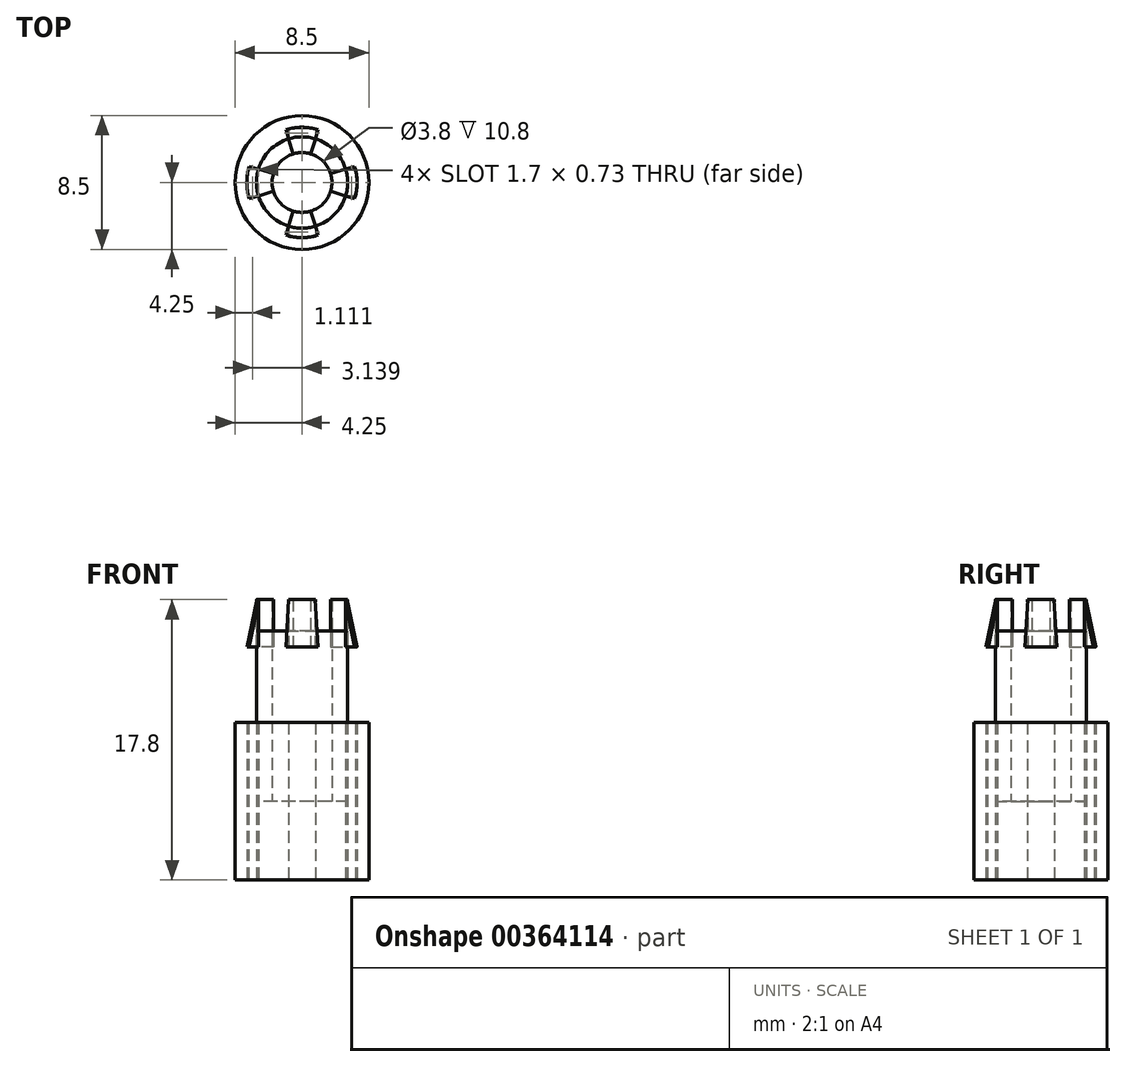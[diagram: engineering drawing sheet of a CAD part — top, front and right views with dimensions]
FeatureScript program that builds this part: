
annotation { "Feature Type Name" : "Feature", "Feature Type Description" : "" }
export const myFeature = defineFeature(function(context is Context, id is Id, definition is map)
    precondition{}
    {
        {
            var Q0;
            Q0=qCreatedBy(makeId("Top.planeOp"),FACE);
            var sketch = newSketch(context, id + "F0", { "sketchPlane" : qUnion([Q0])});
            skCircle(sketch, "E0", {"center": v(0, 0) * mm, "radius": 2.9 * mm});
            skCircle(sketch, "E1", {"center": v(0, 0) * mm, "radius": 4.25 * mm});
            skCircle(sketch, "E2", {"center": v(0, 0) * mm, "radius": 1.9 * mm});
            skLineSegment(sketch, "E3.bottom", {"start": v(-4.25, 4.25) * mm, "end": v(4.25, 4.25) * mm, "construction": true});
            skLineSegment(sketch, "E3.top", {"start": v(-4.25, -4.25) * mm, "end": v(4.25, -4.25) * mm, "construction": true});
            skLineSegment(sketch, "E3.left", {"start": v(-4.25, 4.25) * mm, "end": v(-4.25, -4.25) * mm, "construction": true});
            skLineSegment(sketch, "E3.right", {"start": v(4.25, 4.25) * mm, "end": v(4.25, -4.25) * mm, "construction": true});
            skLineSegment(sketch, "E4", {"start": v(0, 7.12) * mm, "end": v(0, -6.8) * mm, "construction": true});
            skPoint(sketch, "E4.startSnap0", {"position": v(0, 4.25) * mm});
            skLineSegment(sketch, "E5", {"start": v(6.9, 0) * mm, "end": v(-7.5, 0) * mm, "construction": true});
            skArc(sketch, "E6", {"start": v(-0.85, 3.4) * mm, "mid": v(0, 3.5) * mm, "end": v(0.85, 3.4) * mm});
            skArc(sketch, "E7", {"start": v(3.4, 0.85) * mm, "mid": v(3.5, 0) * mm, "end": v(3.4, -0.85) * mm});
            skArc(sketch, "E8", {"start": v(0.85, -3.4) * mm, "mid": v(0, -3.5) * mm, "end": v(-0.85, -3.4) * mm});
            skArc(sketch, "E9", {"start": v(-3.4, -0.85) * mm, "mid": v(-3.5, 0) * mm, "end": v(-3.4, 0.85) * mm});
            skLineSegment(sketch, "E10", {"start": v(-0.85, 3.4) * mm, "end": v(-0.85, 2.77) * mm});
            skLineSegment(sketch, "E11", {"start": v(0.85, 3.4) * mm, "end": v(0.85, 2.77) * mm});
            skLineSegment(sketch, "E12", {"start": v(3.4, 0.85) * mm, "end": v(2.77, 0.85) * mm});
            skLineSegment(sketch, "E13", {"start": v(3.4, -0.85) * mm, "end": v(2.77, -0.85) * mm});
            skLineSegment(sketch, "E14", {"start": v(0.85, -2.77) * mm, "end": v(0.85, -3.4) * mm});
            skLineSegment(sketch, "E15", {"start": v(-0.85, -2.77) * mm, "end": v(-0.85, -3.4) * mm});
            skLineSegment(sketch, "E16", {"start": v(-3.4, 0.85) * mm, "end": v(-2.77, 0.85) * mm});
            skLineSegment(sketch, "E17", {"start": v(-3.4, -0.85) * mm, "end": v(-2.77, -0.85) * mm});
            skLineSegment(sketch, "E18", {"start": v(0, 0) * mm, "end": v(-0.85, 2.77) * mm, "construction": true});
            skLineSegment(sketch, "E19", {"start": v(0, 0) * mm, "end": v(0.85, 2.77) * mm, "construction": true});
            skLineSegment(sketch, "E20", {"start": v(2.77, 0.85) * mm, "end": v(0, 0) * mm, "construction": true});
            skLineSegment(sketch, "E21", {"start": v(0, 0) * mm, "end": v(2.77, -0.85) * mm, "construction": true});
            skLineSegment(sketch, "E22", {"start": v(0, 0) * mm, "end": v(0.85, -2.77) * mm, "construction": true});
            skLineSegment(sketch, "E23", {"start": v(-0.85, -2.77) * mm, "end": v(0, 0) * mm, "construction": true});
            skLineSegment(sketch, "E24", {"start": v(0, 0) * mm, "end": v(-2.77, -0.85) * mm, "construction": true});
            skLineSegment(sketch, "E25", {"start": v(0, 0) * mm, "end": v(-2.77, 0.85) * mm, "construction": true});
            skLineSegment(sketch, "E26", {"start": v(-1.82, 0.56) * mm, "end": v(-2.77, 0.85) * mm});
            skLineSegment(sketch, "E27", {"start": v(-1.82, -0.56) * mm, "end": v(-2.77, -0.85) * mm});
            skLineSegment(sketch, "E28", {"start": v(-0.56, -1.82) * mm, "end": v(-0.85, -2.77) * mm});
            skLineSegment(sketch, "E29", {"start": v(0.85, -2.77) * mm, "end": v(0.56, -1.82) * mm});
            skLineSegment(sketch, "E30", {"start": v(2.77, -0.85) * mm, "end": v(1.82, -0.56) * mm});
            skLineSegment(sketch, "E31", {"start": v(1.82, 0.56) * mm, "end": v(2.77, 0.85) * mm});
            skLineSegment(sketch, "E32", {"start": v(0.56, 1.82) * mm, "end": v(0.85, 2.77) * mm});
            skLineSegment(sketch, "E33", {"start": v(-0.56, 1.82) * mm, "end": v(-0.85, 2.77) * mm});
            skLineSegment(sketch, "E34", {"start": v(0, 0) * mm, "end": v(-4.25, 4.25) * mm, "construction": true});
            skLineSegment(sketch, "E35", {"start": v(0, 0) * mm, "end": v(4.25, 4.25) * mm, "construction": true});
            skLineSegment(sketch, "E36", {"start": v(0, 0) * mm, "end": v(4.25, -4.25) * mm, "construction": true});
            skLineSegment(sketch, "E37", {"start": v(0, 0) * mm, "end": v(-4.25, -4.25) * mm, "construction": true});
            skSolve(sketch);
        }
        {
            var Q0;
            Q0=makeQuery(id+"F0.imprint","IMPRINT",FACE,{"disambiguationData":[TD([[makeQuery(id+"F0.imprint","IMPRINT",EDGE,{"derivedFrom":sQuery(id+"F0.wireOp",EDGE,"E1")}),1.0]])]});
            var Q1;
            {var subQ2=sQuery(id+"F0.wireOp",EDGE,"E30");Q1=makeQuery(id+"F0.imprint","IMPRINT",FACE,{"disambiguationData":[TD([[makeQuery(id+"F0.imprint","IMPRINT",EDGE,{"derivedFrom":subQ2}),-1.0]])]});}
            var Q2;
            {var subQ2=sQuery(id+"F0.wireOp",EDGE,"E31");Q2=makeQuery(id+"F0.imprint","IMPRINT",FACE,{"disambiguationData":[TD([[makeQuery(id+"F0.imprint","IMPRINT",EDGE,{"derivedFrom":subQ2}),1.0]])]});}
            var Q3;
            {var subQ2=sQuery(id+"F0.wireOp",EDGE,"E32");Q3=makeQuery(id+"F0.imprint","IMPRINT",FACE,{"disambiguationData":[TD([[makeQuery(id+"F0.imprint","IMPRINT",EDGE,{"derivedFrom":subQ2}),1.0]])]});}
            var Q4;
            Q4=makeQuery(id+"F0.imprint","IMPRINT",FACE,{"disambiguationData":[TD([[makeQuery(id+"F0.imprint","IMPRINT",EDGE,{"derivedFrom":sQuery(id+"F0.wireOp",EDGE,"E6")}),-1.0]])]});
            var Q5;
            {var subQ2=sQuery(id+"F0.wireOp",EDGE,"E26");Q5=makeQuery(id+"F0.imprint","IMPRINT",FACE,{"disambiguationData":[TD([[makeQuery(id+"F0.imprint","IMPRINT",EDGE,{"derivedFrom":subQ2}),-1.0]])]});}
            var Q6;
            {var subQ0=sQuery(id+"F0.wireOp",EDGE,"E26");Q6=makeQuery(id+"F0.imprint","IMPRINT",FACE,{"disambiguationData":[TD([[makeQuery(id+"F0.imprint","IMPRINT",EDGE,{"derivedFrom":subQ0}),1.0]])]});}
            var Q7;
            Q7=makeQuery(id+"F0.imprint","IMPRINT",FACE,{"disambiguationData":[TD([[makeQuery(id+"F0.imprint","IMPRINT",EDGE,{"derivedFrom":sQuery(id+"F0.wireOp",EDGE,"E9")}),-1.0]])]});
            var Q8;
            {var subQ2=sQuery(id+"F0.wireOp",EDGE,"E27");Q8=makeQuery(id+"F0.imprint","IMPRINT",FACE,{"disambiguationData":[TD([[makeQuery(id+"F0.imprint","IMPRINT",EDGE,{"derivedFrom":subQ2}),1.0]])]});}
            var Q9;
            {var subQ2=sQuery(id+"F0.wireOp",EDGE,"E28");Q9=makeQuery(id+"F0.imprint","IMPRINT",FACE,{"disambiguationData":[TD([[makeQuery(id+"F0.imprint","IMPRINT",EDGE,{"derivedFrom":subQ2}),1.0]])]});}
            var Q10;
            Q10=makeQuery(id+"F0.imprint","IMPRINT",FACE,{"disambiguationData":[TD([[makeQuery(id+"F0.imprint","IMPRINT",EDGE,{"derivedFrom":sQuery(id+"F0.wireOp",EDGE,"E8")}),-1.0]])]});
            var Q11;
            {var subQ2=sQuery(id+"F0.wireOp",EDGE,"E29");Q11=makeQuery(id+"F0.imprint","IMPRINT",FACE,{"disambiguationData":[TD([[makeQuery(id+"F0.imprint","IMPRINT",EDGE,{"derivedFrom":subQ2}),-1.0]])]});}
            var Q12;
            {var subQ0=sQuery(id+"F0.wireOp",EDGE,"E2");var subQ5=makeQuery(id+"F0.imprint","INTERSECT",VERTEX,{"derivedFrom":[subQ0,sQuery(id+"F0.wireOp",EDGE,"E31")]});Q12=makeQuery(id+"F0.imprint","IMPRINT",FACE,{"disambiguationData":[TD([[makeQuery(id+"F0.imprint","IMPRINT",EDGE,{"disambiguationData":[TD([[subQ5,-1.0]])],"derivedFrom":subQ0}),1.0]])]});}
            var Q13;
            Q13=makeQuery(id+"F0.imprint","IMPRINT",FACE,{"disambiguationData":[TD([[makeQuery(id+"F0.imprint","IMPRINT",EDGE,{"derivedFrom":sQuery(id+"F0.wireOp",EDGE,"E7")}),-1.0]])]});
            extrude(context, id + "F1", {"entities" : qUnion([Q0, Q1, Q2, Q3, Q4, Q5, Q6, Q7, Q8, Q9, Q10, Q11, Q12, Q13]), "endBound" : BoundingType.SYMMETRIC, "depth" : 10 * mm});
        }
        {
            var Q0;
            {var subQ2=sQuery(id+"F0.wireOp",EDGE,"E29");Q0=makeQuery(id+"F0.imprint","IMPRINT",FACE,{"disambiguationData":[TD([[makeQuery(id+"F0.imprint","IMPRINT",EDGE,{"derivedFrom":subQ2}),-1.0]])]});}
            var Q1;
            {var subQ2=sQuery(id+"F0.wireOp",EDGE,"E28");Q1=makeQuery(id+"F0.imprint","IMPRINT",FACE,{"disambiguationData":[TD([[makeQuery(id+"F0.imprint","IMPRINT",EDGE,{"derivedFrom":subQ2}),1.0]])]});}
            var Q2;
            {var subQ2=sQuery(id+"F0.wireOp",EDGE,"E27");Q2=makeQuery(id+"F0.imprint","IMPRINT",FACE,{"disambiguationData":[TD([[makeQuery(id+"F0.imprint","IMPRINT",EDGE,{"derivedFrom":subQ2}),1.0]])]});}
            var Q3;
            {var subQ2=sQuery(id+"F0.wireOp",EDGE,"E30");Q3=makeQuery(id+"F0.imprint","IMPRINT",FACE,{"disambiguationData":[TD([[makeQuery(id+"F0.imprint","IMPRINT",EDGE,{"derivedFrom":subQ2}),-1.0]])]});}
            var Q4;
            {var subQ2=sQuery(id+"F0.wireOp",EDGE,"E31");Q4=makeQuery(id+"F0.imprint","IMPRINT",FACE,{"disambiguationData":[TD([[makeQuery(id+"F0.imprint","IMPRINT",EDGE,{"derivedFrom":subQ2}),1.0]])]});}
            var Q5;
            {var subQ2=sQuery(id+"F0.wireOp",EDGE,"E32");Q5=makeQuery(id+"F0.imprint","IMPRINT",FACE,{"disambiguationData":[TD([[makeQuery(id+"F0.imprint","IMPRINT",EDGE,{"derivedFrom":subQ2}),1.0]])]});}
            var Q6;
            {var subQ2=sQuery(id+"F0.wireOp",EDGE,"E26");Q6=makeQuery(id+"F0.imprint","IMPRINT",FACE,{"disambiguationData":[TD([[makeQuery(id+"F0.imprint","IMPRINT",EDGE,{"derivedFrom":subQ2}),-1.0]])]});}
            var Q7;
            {var subQ0=sQuery(id+"F0.wireOp",EDGE,"E26");Q7=makeQuery(id+"F0.imprint","IMPRINT",FACE,{"disambiguationData":[TD([[makeQuery(id+"F0.imprint","IMPRINT",EDGE,{"derivedFrom":subQ0}),1.0]])]});}
            extrude(context, id + "F2", {"entities" : qUnion([Q0, Q1, Q2, Q3, Q4, Q5, Q6, Q7]), "depth" : 10.8 * mm});
        }
        {
            var Q0;
            Q0=qCreatedBy(makeId("Top.planeOp"),FACE);
            cPlane(context, id + "F3", {"entities" : qUnion([Q0]), "cplaneType" : CPlaneType.OFFSET, "offset" : 9.8 * mm, "width" : 150 * mm, "height" : 150 * mm});
        }
        {
            var Q0;
            Q0=qCreatedBy(id+"F3.planeOp",FACE);
            var sketch = newSketch(context, id + "F4", { "sketchPlane" : qUnion([Q0])});
            skCircle(sketch, "E38", {"center": v(0, 0) * mm, "radius": 2.9 * mm});
            skCircle(sketch, "E39", {"center": v(0, 0) * mm, "radius": 4.25 * mm});
            skCircle(sketch, "E40", {"center": v(0, 0) * mm, "radius": 1.9 * mm});
            skLineSegment(sketch, "E41.bottom", {"start": v(-4.25, 4.25) * mm, "end": v(4.25, 4.25) * mm, "construction": true});
            skLineSegment(sketch, "E41.top", {"start": v(-4.25, -4.25) * mm, "end": v(4.25, -4.25) * mm, "construction": true});
            skLineSegment(sketch, "E41.left", {"start": v(-4.25, 4.25) * mm, "end": v(-4.25, -4.25) * mm, "construction": true});
            skLineSegment(sketch, "E41.right", {"start": v(4.25, 4.25) * mm, "end": v(4.25, -4.25) * mm, "construction": true});
            skLineSegment(sketch, "E42", {"start": v(0, 7.12) * mm, "end": v(0, -6.8) * mm, "construction": true});
            skPoint(sketch, "E42.startSnap0", {"position": v(0, 4.25) * mm});
            skLineSegment(sketch, "E43", {"start": v(6.9, 0) * mm, "end": v(-7.5, 0) * mm, "construction": true});
            skArc(sketch, "E44", {"start": v(-0.85, 3.4) * mm, "mid": v(0, 3.5) * mm, "end": v(0.85, 3.4) * mm});
            skArc(sketch, "E45", {"start": v(3.4, 0.85) * mm, "mid": v(3.5, 0) * mm, "end": v(3.4, -0.85) * mm});
            skArc(sketch, "E46", {"start": v(0.85, -3.4) * mm, "mid": v(0, -3.5) * mm, "end": v(-0.85, -3.4) * mm});
            skArc(sketch, "E47", {"start": v(-3.4, -0.85) * mm, "mid": v(-3.5, 0) * mm, "end": v(-3.4, 0.85) * mm});
            skLineSegment(sketch, "E48", {"start": v(-0.85, 3.4) * mm, "end": v(-0.85, 2.77) * mm});
            skLineSegment(sketch, "E49", {"start": v(0.85, 3.4) * mm, "end": v(0.85, 2.77) * mm});
            skLineSegment(sketch, "E50", {"start": v(3.4, 0.85) * mm, "end": v(2.77, 0.85) * mm});
            skLineSegment(sketch, "E51", {"start": v(3.4, -0.85) * mm, "end": v(2.77, -0.85) * mm});
            skLineSegment(sketch, "E52", {"start": v(0.85, -2.77) * mm, "end": v(0.85, -3.4) * mm});
            skLineSegment(sketch, "E53", {"start": v(-0.85, -2.77) * mm, "end": v(-0.85, -3.4) * mm});
            skLineSegment(sketch, "E54", {"start": v(-3.4, 0.85) * mm, "end": v(-2.77, 0.85) * mm});
            skLineSegment(sketch, "E55", {"start": v(-3.4, -0.85) * mm, "end": v(-2.77, -0.85) * mm});
            skLineSegment(sketch, "E56", {"start": v(0, 0) * mm, "end": v(-0.85, 2.77) * mm, "construction": true});
            skLineSegment(sketch, "E57", {"start": v(0, 0) * mm, "end": v(0.85, 2.77) * mm, "construction": true});
            skLineSegment(sketch, "E58", {"start": v(2.77, 0.85) * mm, "end": v(0, 0) * mm, "construction": true});
            skLineSegment(sketch, "E59", {"start": v(0, 0) * mm, "end": v(2.77, -0.85) * mm, "construction": true});
            skLineSegment(sketch, "E60", {"start": v(0, 0) * mm, "end": v(0.85, -2.77) * mm, "construction": true});
            skLineSegment(sketch, "E61", {"start": v(-0.85, -2.77) * mm, "end": v(0, 0) * mm, "construction": true});
            skLineSegment(sketch, "E62", {"start": v(0, 0) * mm, "end": v(-2.77, -0.85) * mm, "construction": true});
            skLineSegment(sketch, "E63", {"start": v(0, 0) * mm, "end": v(-2.77, 0.85) * mm, "construction": true});
            skLineSegment(sketch, "E64", {"start": v(-1.82, 0.56) * mm, "end": v(-2.77, 0.85) * mm});
            skLineSegment(sketch, "E65", {"start": v(-1.82, -0.56) * mm, "end": v(-2.77, -0.85) * mm});
            skLineSegment(sketch, "E66", {"start": v(-0.56, -1.82) * mm, "end": v(-0.85, -2.77) * mm});
            skLineSegment(sketch, "E67", {"start": v(0.85, -2.77) * mm, "end": v(0.56, -1.82) * mm});
            skLineSegment(sketch, "E68", {"start": v(2.77, -0.85) * mm, "end": v(1.82, -0.56) * mm});
            skLineSegment(sketch, "E69", {"start": v(1.82, 0.56) * mm, "end": v(2.77, 0.85) * mm});
            skLineSegment(sketch, "E70", {"start": v(0.56, 1.82) * mm, "end": v(0.85, 2.77) * mm});
            skLineSegment(sketch, "E71", {"start": v(-0.56, 1.82) * mm, "end": v(-0.85, 2.77) * mm});
            skLineSegment(sketch, "E72", {"start": v(0, 0) * mm, "end": v(-4.25, 4.25) * mm, "construction": true});
            skLineSegment(sketch, "E73", {"start": v(0, 0) * mm, "end": v(4.25, 4.25) * mm, "construction": true});
            skLineSegment(sketch, "E74", {"start": v(0, 0) * mm, "end": v(4.25, -4.25) * mm, "construction": true});
            skLineSegment(sketch, "E75", {"start": v(0, 0) * mm, "end": v(-4.25, -4.25) * mm, "construction": true});
            skSolve(sketch);
        }
        {
            var Q0;
            {var subQ2=sQuery(id+"F4.wireOp",EDGE,"E70");Q0=makeQuery(id+"F4.imprint","IMPRINT",FACE,{"disambiguationData":[TD([[makeQuery(id+"F4.imprint","IMPRINT",EDGE,{"derivedFrom":subQ2}),1.0]])]});}
            var Q1;
            {var subQ0=sQuery(id+"F4.wireOp",EDGE,"E64");Q1=makeQuery(id+"F4.imprint","IMPRINT",FACE,{"disambiguationData":[TD([[makeQuery(id+"F4.imprint","IMPRINT",EDGE,{"derivedFrom":subQ0}),1.0]])]});}
            var Q2;
            {var subQ2=sQuery(id+"F4.wireOp",EDGE,"E66");Q2=makeQuery(id+"F4.imprint","IMPRINT",FACE,{"disambiguationData":[TD([[makeQuery(id+"F4.imprint","IMPRINT",EDGE,{"derivedFrom":subQ2}),1.0]])]});}
            var Q3;
            {var subQ2=sQuery(id+"F4.wireOp",EDGE,"E68");Q3=makeQuery(id+"F4.imprint","IMPRINT",FACE,{"disambiguationData":[TD([[makeQuery(id+"F4.imprint","IMPRINT",EDGE,{"derivedFrom":subQ2}),-1.0]])]});}
            extrude(context, id + "F5", {"entities" : qUnion([Q0, Q1, Q2, Q3]), "depth" : 3 * mm});
        }
        {
            var Q0;
            Q0=qCreatedBy(makeId("Front.planeOp"),FACE);
            var sketch = newSketch(context, id + "F6", { "sketchPlane" : qUnion([Q0])});
            skLineSegment(sketch, "E76", {"start": v(0, 15.19) * mm, "end": v(0, -1.9) * mm, "construction": true});
            skLineSegment(sketch, "E77.0", {"start": v(-3.5, 15.19) * mm, "end": v(-3.5, -1.9) * mm, "construction": true});
            skLineSegment(sketch, "E78.MirrorCS", {"start": v(3.5, 15.19) * mm, "end": v(3.5, -1.9) * mm, "construction": true});
            skLineSegment(sketch, "E79", {"start": v(3.5, 12.8) * mm, "end": v(2.88, 12.8) * mm, "construction": true});
            skLineSegment(sketch, "E80", {"start": v(5.77, 9.8) * mm, "end": v(-5.74, 9.8) * mm, "construction": true});
            skLineSegment(sketch, "E81", {"start": v(2.88, 12.8) * mm, "end": v(2.88, 9.8) * mm});
            skLineSegment(sketch, "E82", {"start": v(2.88, 9.8) * mm, "end": v(3.5, 9.8) * mm});
            skLineSegment(sketch, "E83", {"start": v(2.88, 12.8) * mm, "end": v(3.5, 9.8) * mm});
            skLineSegment(sketch, "E84.MirrorCS", {"start": v(-2.88, 12.8) * mm, "end": v(-2.88, 9.8) * mm});
            skLineSegment(sketch, "E85.MirrorCS", {"start": v(-2.88, 12.8) * mm, "end": v(-3.5, 9.8) * mm});
            skLineSegment(sketch, "E86", {"start": v(3.5, 9.8) * mm, "end": v(2.88, 9.8) * mm});
            skLineSegment(sketch, "E87", {"start": v(-2.88, 9.8) * mm, "end": v(-3.5, 9.8) * mm});
            skSolve(sketch);
        }
        {
            var Q0;
            Q0=qCreatedBy(makeId("Right.planeOp"),FACE);
            var sketch = newSketch(context, id + "F7", { "sketchPlane" : qUnion([Q0])});
            skLineSegment(sketch, "E88", {"start": v(0, 15.19) * mm, "end": v(0, -1.9) * mm, "construction": true});
            skLineSegment(sketch, "E89.0", {"start": v(-3.5, 15.19) * mm, "end": v(-3.5, -1.9) * mm, "construction": true});
            skLineSegment(sketch, "E90.MirrorCS", {"start": v(3.5, 15.19) * mm, "end": v(3.5, -1.9) * mm, "construction": true});
            skLineSegment(sketch, "E91", {"start": v(3.5, 12.8) * mm, "end": v(2.88, 12.8) * mm, "construction": true});
            skLineSegment(sketch, "E92", {"start": v(5.77, 9.8) * mm, "end": v(-5.74, 9.8) * mm, "construction": true});
            skLineSegment(sketch, "E93", {"start": v(2.88, 12.8) * mm, "end": v(2.88, 9.8) * mm});
            skLineSegment(sketch, "E94", {"start": v(2.88, 9.8) * mm, "end": v(3.5, 9.8) * mm});
            skLineSegment(sketch, "E95", {"start": v(2.88, 12.8) * mm, "end": v(3.5, 9.8) * mm});
            skLineSegment(sketch, "E96.MirrorCS", {"start": v(-2.88, 12.8) * mm, "end": v(-2.88, 9.8) * mm});
            skLineSegment(sketch, "E97.MirrorCS", {"start": v(-2.88, 12.8) * mm, "end": v(-3.5, 9.8) * mm});
            skLineSegment(sketch, "E98", {"start": v(3.5, 9.8) * mm, "end": v(2.88, 9.8) * mm});
            skLineSegment(sketch, "E99", {"start": v(-2.88, 9.8) * mm, "end": v(-3.5, 9.8) * mm});
            skSolve(sketch);
        }
        {
            var Q0;
            Q0=makeQuery(id+"F6.imprint","IMPRINT",FACE,{"disambiguationData":[TD([[makeQuery(id+"F6.imprint","IMPRINT",EDGE,{"derivedFrom":sQuery(id+"F6.wireOp",EDGE,"E81")}),1.0]])]});
            var Q1;
            Q1=makeQuery(id+"F6.imprint","IMPRINT",FACE,{"disambiguationData":[TD([[makeQuery(id+"F6.imprint","IMPRINT",EDGE,{"derivedFrom":sQuery(id+"F6.wireOp",EDGE,"E84.MirrorCS")}),-1.0]])]});
            var Q2;
            Q2=makeQuery(id+"F7.imprint","IMPRINT",FACE,{"disambiguationData":[TD([[makeQuery(id+"F7.imprint","IMPRINT",EDGE,{"derivedFrom":sQuery(id+"F7.wireOp",EDGE,"E93")}),1.0]])]});
            var Q3;
            Q3=makeQuery(id+"F7.imprint","IMPRINT",FACE,{"disambiguationData":[TD([[makeQuery(id+"F7.imprint","IMPRINT",EDGE,{"derivedFrom":sQuery(id+"F7.wireOp",EDGE,"E96.MirrorCS")}),-1.0]])]});
            var Q4;
            Q4=sQuery(id+"F6.wireOp",EDGE,"E76");
            revolve(context, id + "F8", {"entities" : qUnion([Q0, Q1, Q2, Q3]), "axis" : qUnion([Q4]), "revolveType" : RevolveType.SYMMETRIC, "angle" : 34 * degree});
        }
    });
